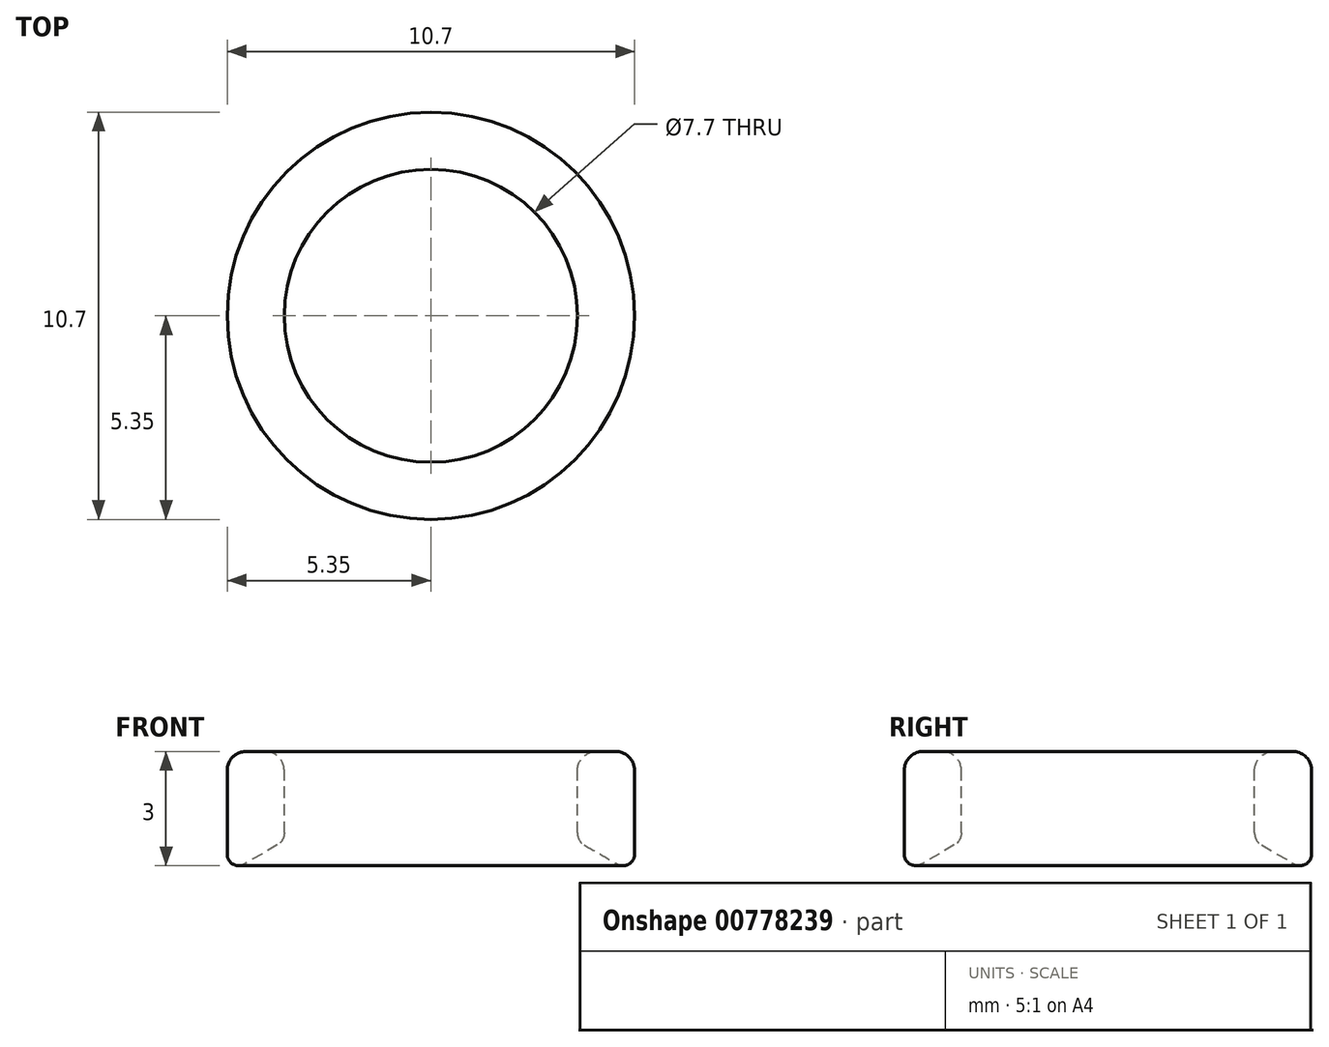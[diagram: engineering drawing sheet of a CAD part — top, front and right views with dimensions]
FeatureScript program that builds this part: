
annotation { "Feature Type Name" : "Feature", "Feature Type Description" : "" }
export const myFeature = defineFeature(function(context is Context, id is Id, definition is map)
    precondition{}
    {
        {
            var Q0;
            Q0=qCreatedBy(makeId("Front.planeOp"),FACE);
            var sketch = newSketch(context, id + "F0", { "sketchPlane" : qUnion([Q0])});
            skLineSegment(sketch, "E0", {"start": v(0, 10.59) * mm, "end": v(0, -11.76) * mm, "construction": true});
            skCircle(sketch, "E1", {"center": v(0, 0) * mm, "radius": 8.5 * mm, "construction": true});
            skCircle(sketch, "E2.0", {"center": v(0, 0) * mm, "radius": 8.2 * mm, "construction": true});
            skLineSegment(sketch, "E3", {"start": v(-4.03, 8.12) * mm, "end": v(-4.9, 7.62) * mm});
            skArc(sketch, "E4", {"start": v(-5.35, 7.88) * mm, "mid": v(-5.2, 7.62) * mm, "end": v(-4.9, 7.62) * mm});
            skLineSegment(sketch, "E5", {"start": v(-5.35, 7.88) * mm, "end": v(-5.35, 10.58) * mm});
            skLineSegment(sketch, "E6", {"start": v(-3.75, 0) * mm, "end": v(-3.75, 14.65) * mm, "construction": true});
            skArc(sketch, "E7", {"start": v(-4.03, 8.12) * mm, "mid": v(-3.9, 8.26) * mm, "end": v(-3.85, 8.44) * mm});
            skLineSegment(sketch, "E8", {"start": v(-3.85, 8.44) * mm, "end": v(-3.85, 10.58) * mm});
            skLineSegment(sketch, "E9", {"start": v(-5.35, 10.58) * mm, "end": v(-3.85, 10.58) * mm});
            skSolve(sketch);
        }
        {
            var Q0;
            Q0 = qSketchRegion(id + "F0", true);
            var Q1;
            Q1=sQuery(id+"F0.wireOp",EDGE,"E0");
            revolve(context, id + "F1", {"surfaceOperationType" : NewSurfaceOperationType.NEW, "entities" : qUnion([Q0]), "axis" : qUnion([Q1]), "revolveType" : RevolveType.FULL});
        }
        {
            var Q0;
            Q0=makeQuery(id+"F1.opRevolve","SWEPT_FACE",FACE,{"disambiguationData":[OSD([sQuery(id+"F0.wireOp",EDGE,"E9")])]});
            fillet(context, id + "F2", {"entities" : qUnion([Q0]), "radius" : 0.5 * mm, "tangentPropagation" : true, "allowEdgeOverflow" : false});
        }
    });
